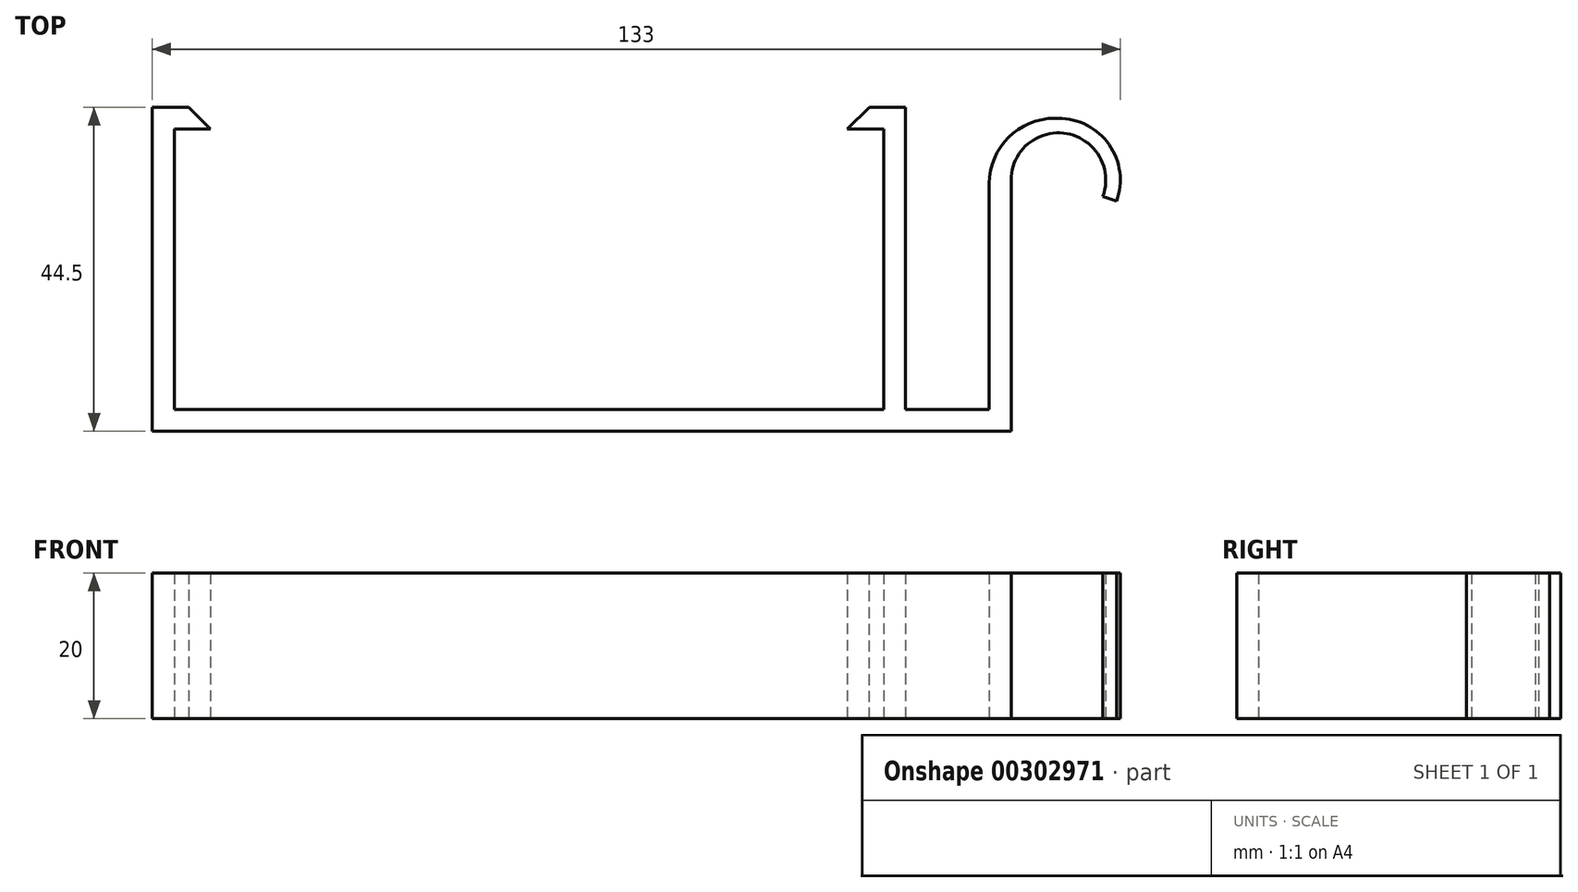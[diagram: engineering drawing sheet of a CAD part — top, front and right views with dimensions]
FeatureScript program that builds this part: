
annotation { "Feature Type Name" : "Feature", "Feature Type Description" : "" }
export const myFeature = defineFeature(function(context is Context, id is Id, definition is map)
    precondition{}
    {
        {
            var Q0;
            Q0=qCreatedBy(makeId("Top.planeOp"),FACE);
            var sketch = newSketch(context, id + "F0", { "sketchPlane" : qUnion([Q0])});
            skLineSegment(sketch, "E0", {"start": v(0, 0) * mm, "end": v(0, 40) * mm});
            skLineSegment(sketch, "E1", {"start": v(0, 0) * mm, "end": v(-11.5, 0) * mm});
            skLineSegment(sketch, "E2", {"start": v(-112, 0) * mm, "end": v(-112, 38.5) * mm});
            skLineSegment(sketch, "E3", {"start": v(-14.5, 0) * mm, "end": v(-14.5, 38.5) * mm});
            skLineSegment(sketch, "E4", {"start": v(-112, 38.5) * mm, "end": v(-107, 38.5) * mm});
            skLineSegment(sketch, "E5", {"start": v(-14.5, 38.5) * mm, "end": v(-19.5, 38.5) * mm});
            skLineSegment(sketch, "E6.0", {"start": v(-115, 41.5) * mm, "end": v(-107, 41.5) * mm});
            skLineSegment(sketch, "E6.1", {"start": v(-115, -3) * mm, "end": v(-115, 41.5) * mm});
            skLineSegment(sketch, "E6.2", {"start": v(3, -3) * mm, "end": v(-115, -3) * mm});
            skLineSegment(sketch, "E6.3", {"start": v(3, -3) * mm, "end": v(3, 31.5) * mm});
            skLineSegment(sketch, "E7.0", {"start": v(-11.5, 41.5) * mm, "end": v(-19.5, 41.5) * mm});
            skLineSegment(sketch, "E7.1", {"start": v(-11.5, 0) * mm, "end": v(-11.5, 41.5) * mm});
            skLineSegment(sketch, "E8", {"start": v(-107, 41.5) * mm, "end": v(-107, 38.5) * mm});
            skLineSegment(sketch, "E9", {"start": v(-19.5, 41.5) * mm, "end": v(-19.5, 38.5) * mm});
            skLineSegment(sketch, "E10", {"start": v(0, 40) * mm, "end": v(3, 40) * mm});
            skLineSegment(sketch, "E11", {"start": v(3, 40) * mm, "end": v(9.5, 40) * mm});
            skLineSegment(sketch, "E12", {"start": v(9.5, 40) * mm, "end": v(9.5, 31.5) * mm, "construction": true});
            skArc(sketch, "E13", {"start": v(15.6, 29.28) * mm, "mid": v(10.63, 37.9) * mm, "end": v(3, 31.5) * mm});
            skArc(sketch, "E14", {"start": v(17.49, 28.6) * mm, "mid": v(16.46, 36.38) * mm, "end": v(9.5, 40) * mm});
            skLineSegment(sketch, "E15", {"start": v(9.5, 31.5) * mm, "end": v(18, 31.5) * mm, "construction": true});
            skLineSegment(sketch, "E16", {"start": v(15.6, 29.28) * mm, "end": v(17.49, 28.6) * mm});
            skLineSegment(sketch, "E17.trimOffspring", {"start": v(-14.5, 0) * mm, "end": v(-112, 0) * mm});
            skSolve(sketch);
        }
        {
            var Q0;
            Q0=makeQuery(id+"F0.imprint","IMPRINT",FACE,{"disambiguationData":[TD([[makeQuery(id+"F0.imprint","IMPRINT",EDGE,{"derivedFrom":sQuery(id+"F0.wireOp",EDGE,"E0")}),-1.0]])]});
            extrude(context, id + "F1", {"entities" : qUnion([Q0]), "depth" : 20 * mm, "offsetDistance" : 25 * mm});
        }
        {
            var Q0;
            Q0=makeQuery(id+"F1.opExtrude","SWEPT_EDGE",EDGE,{"disambiguationData":[OSD([sQuery(id+"F0.wireOp",EDGE,"E6.0"),sQuery(id+"F0.wireOp",EDGE,"E8")])]});
            var Q1;
            Q1=makeQuery(id+"F1.opExtrude","SWEPT_EDGE",EDGE,{"disambiguationData":[OSD([sQuery(id+"F0.wireOp",EDGE,"E7.0"),sQuery(id+"F0.wireOp",EDGE,"E9")])]});
            chamfer(context, id + "F2", {"entities" : qUnion([Q0, Q1]), "width" : 3 * mm, "tangentPropagation" : true});
        }
        {
            var Q0;
            Q0=makeQuery(id+"F1.opExtrude","SWEPT_EDGE",EDGE,{"disambiguationData":[OSD([sQuery(id+"F0.wireOp",EDGE,"E0"),sQuery(id+"F0.wireOp",EDGE,"E10")])]});
            fillet(context, id + "F3", {"entities" : qUnion([Q0]), "radius" : 9 * mm, "tangentPropagation" : true, "allowEdgeOverflow" : false});
        }
    });
